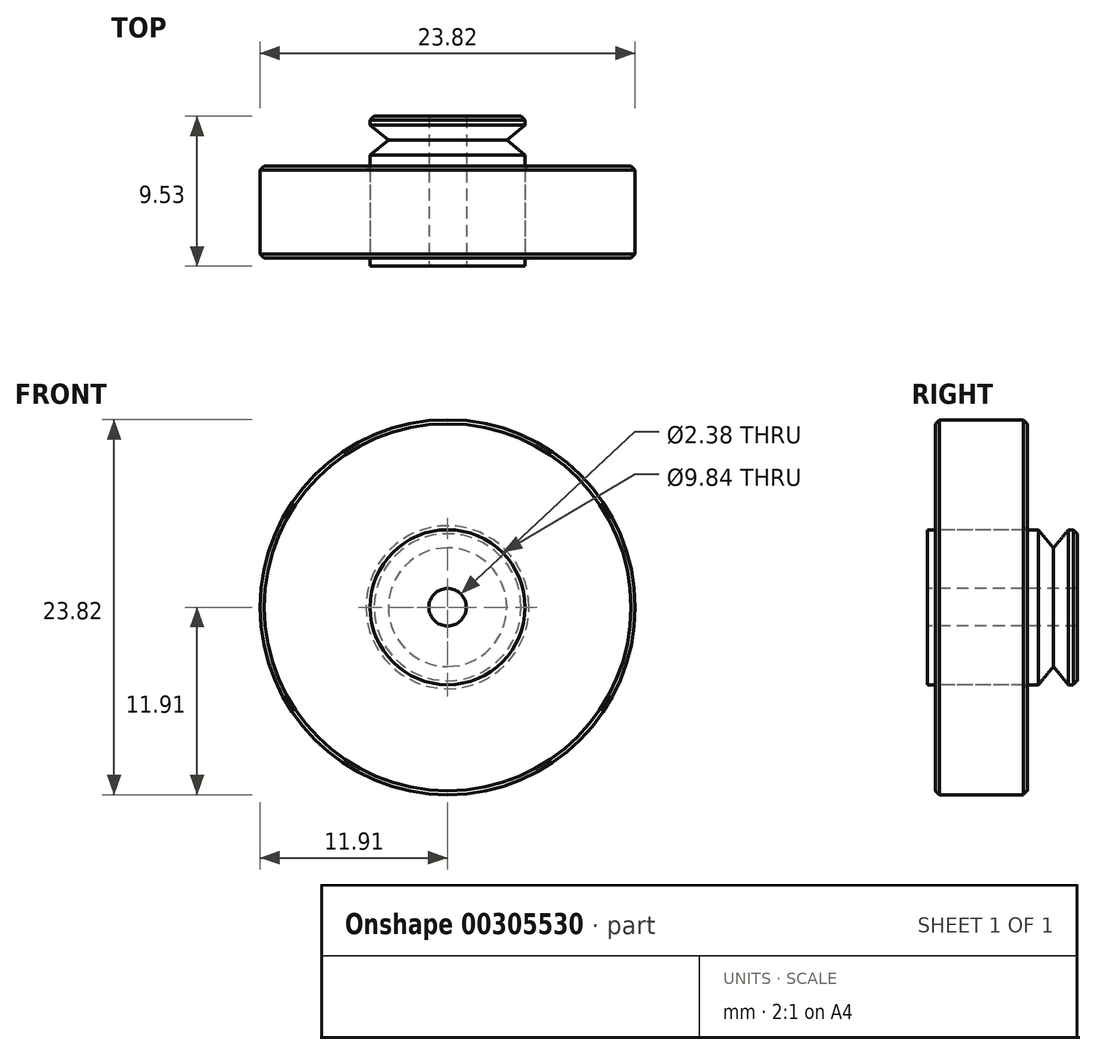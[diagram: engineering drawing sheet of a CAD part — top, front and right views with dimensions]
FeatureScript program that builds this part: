
annotation { "Feature Type Name" : "Feature", "Feature Type Description" : "" }
export const myFeature = defineFeature(function(context is Context, id is Id, definition is map)
    precondition{}
    {
        {
            var Q0;
            Q0=qCreatedBy(makeId("Front.planeOp"),FACE);
            var sketch = newSketch(context, id + "F0", { "sketchPlane" : qUnion([Q0])});
            skCircle(sketch, "E0", {"center": v(0, 0) * mm, "radius": 1.2 * mm});
            skCircle(sketch, "E1", {"center": v(0, 0) * mm, "radius": 11.9 * mm});
            skCircle(sketch, "E2", {"center": v(0, 0) * mm, "radius": 4.92 * mm});
            skSolve(sketch);
        }
        {
            var Q0;
            Q0=makeQuery(id+"F0.imprint","IMPRINT",FACE,{"disambiguationData":[TD([[makeQuery(id+"F0.imprint","IMPRINT",EDGE,{"derivedFrom":sQuery(id+"F0.wireOp",EDGE,"E1")}),1.0]])]});
            extrude(context, id + "F1", {"entities" : qUnion([Q0]), "oppositeDirection" : true, "depth" : 6.35 * mm, "hasSecondDirection" : true, "secondDirectionOppositeDirection" : true, "secondDirectionDepth" : 0.5 * mm});
        }
        {
            var Q0;
            Q0=makeQuery(id+"F0.imprint","IMPRINT",FACE,{"disambiguationData":[TD([[makeQuery(id+"F0.imprint","IMPRINT",EDGE,{"derivedFrom":sQuery(id+"F0.wireOp",EDGE,"E0")}),-1.0]])]});
            extrude(context, id + "F2", {"entities" : qUnion([Q0]), "oppositeDirection" : true, "depth" : 9.52 * mm});
        }
        {
            var Q0;
            Q0=makeQuery(id+"F1.opExtrude","CAP_EDGE",EDGE,{"disambiguationData":[OSD([sQuery(id+"F0.wireOp",EDGE,"E1")])],"isStart":false});
            var Q1;
            Q1=makeQuery(id+"F1.opExtrude","CAP_EDGE",EDGE,{"disambiguationData":[OSD([sQuery(id+"F0.wireOp",EDGE,"E1")])],"isStart":true});
            var Q2;
            Q2=makeQuery(id+"F2.opExtrude","CAP_EDGE",EDGE,{"disambiguationData":[OSD([sQuery(id+"F0.wireOp",EDGE,"E2")])],"isStart":false});
            var Q3;
            Q3=makeQuery(id+"F1.opExtrude","CAP_EDGE",EDGE,{"disambiguationData":[OSD([sQuery(id+"F0.wireOp",EDGE,"E2")])],"isStart":false});
            chamfer(context, id + "F3", {"entities" : qUnion([Q0, Q1, Q2, Q3]), "width" : 0.25 * mm, "tangentPropagation" : true});
        }
        {
            var Q0;
            Q0=qCreatedBy(makeId("Right.planeOp"),FACE);
            var sketch = newSketch(context, id + "F4", { "sketchPlane" : qUnion([Q0])});
            skLineSegment(sketch, "E3", {"start": v(8.02, 3.76) * mm, "end": v(6.52, 5.59) * mm});
            skLineSegment(sketch, "E4", {"start": v(6.52, 5.59) * mm, "end": v(9.53, 5.59) * mm});
            skLineSegment(sketch, "E5", {"start": v(9.53, 5.59) * mm, "end": v(8.02, 3.76) * mm});
            skSolve(sketch);
        }
        {
            var Q0;
            Q0=makeQuery(id+"F4.imprint","IMPRINT",FACE,{"disambiguationData":[TD([[makeQuery(id+"F4.imprint","IMPRINT",EDGE,{"derivedFrom":sQuery(id+"F4.wireOp",EDGE,"E3")}),-1.0]])]});
            var Q1;
            Q1=makeQuery(id+"F2.opExtrude","SWEPT_FACE",FACE,{"disambiguationData":[OSD([sQuery(id+"F0.wireOp",EDGE,"E0")])]});
            revolve(context, id + "F5", {"operationType" : NewBodyOperationType.REMOVE, "entities" : qUnion([Q0]), "axis" : qUnion([Q1]), "revolveType" : RevolveType.FULL, "oppositeDirection" : true});
        }
    });
